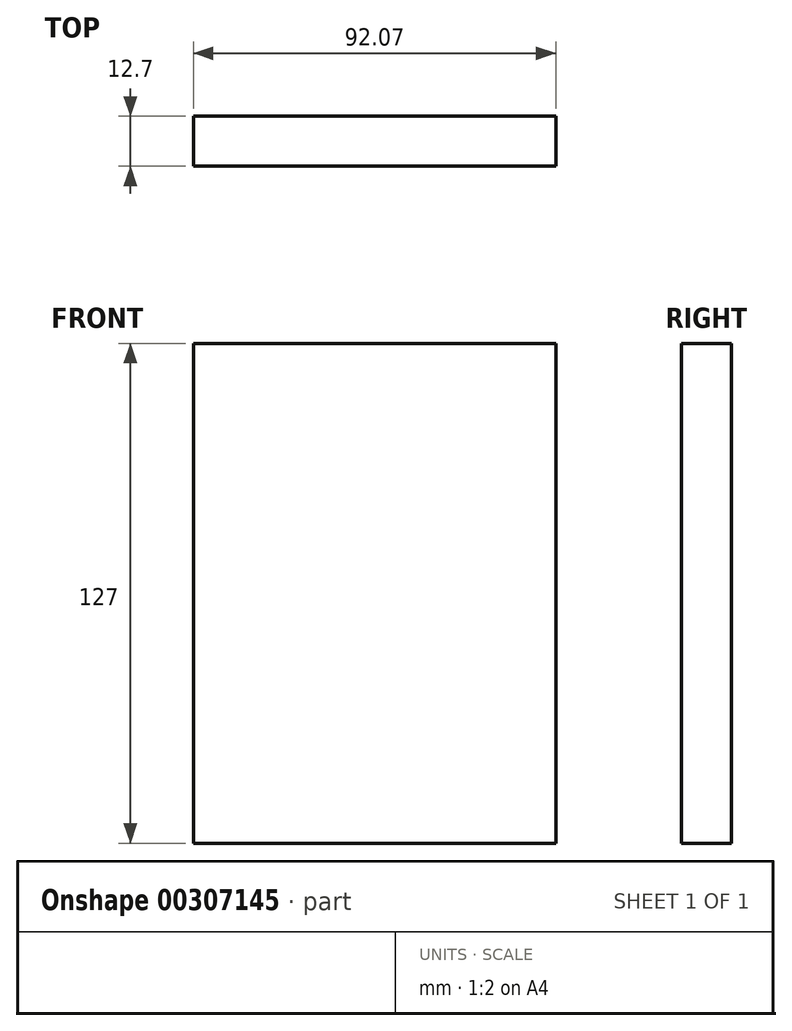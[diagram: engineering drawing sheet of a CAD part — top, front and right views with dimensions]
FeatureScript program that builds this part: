
annotation { "Feature Type Name" : "Feature", "Feature Type Description" : "" }
export const myFeature = defineFeature(function(context is Context, id is Id, definition is map)
    precondition{}
    {
        {
            var Q0;
            Q0=qCreatedBy(makeId("Front.planeOp"),FACE);
            var sketch = newSketch(context, id + "F0", { "sketchPlane" : qUnion([Q0])});
            skLineSegment(sketch, "E0.bottom", {"start": v(-42.28, 78.99) * mm, "end": v(49.8, 78.99) * mm});
            skLineSegment(sketch, "E0.top", {"start": v(-42.28, -48.01) * mm, "end": v(49.8, -48.01) * mm});
            skLineSegment(sketch, "E0.left", {"start": v(-42.28, 78.99) * mm, "end": v(-42.28, -48.01) * mm});
            skLineSegment(sketch, "E0.right", {"start": v(49.8, 78.99) * mm, "end": v(49.8, -48.01) * mm});
            skSolve(sketch);
        }
        {
            var Q0;
            Q0 = qSketchRegion(id + "F0", true);
            extrude(context, id + "F1", {"entities" : qUnion([Q0]), "depth" : 12.7 * mm});
        }
    });
